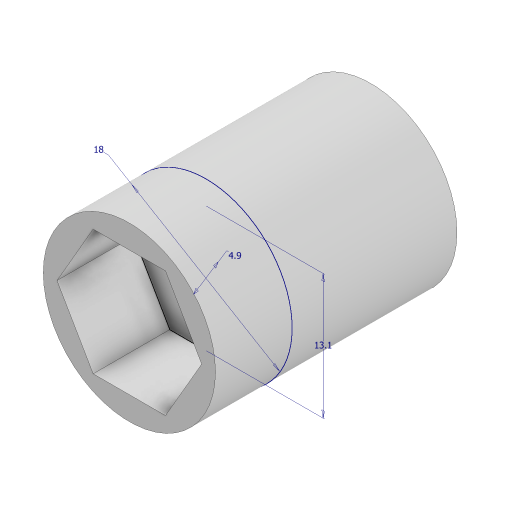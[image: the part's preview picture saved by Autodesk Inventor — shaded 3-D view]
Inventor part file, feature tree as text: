
AUTODESK INVENTOR PART (.ipt)
format: ipt  version: 2023 (Build 270158000, 158)  size: 139,264 bytes
history: native  units: mm
features: extrude x3, sketch x2
ambient origin geometry x8: Origin, YZ Plane, XZ Plane, XY Plane, X Axis, Y Axis, Z Axis, Center Point
bodies: Solid1 (feature_tree)
feature tree (5):
  sketch  "Sketch1"  dims[d0=13.1mm d1=18.0mm]
  extrude  "Extrusion1"  Depth=13.1mm
  extrude  "Extrusion2"  Depth=8.0mm TaperAngle=0.0deg
  extrude  "Extrusion3"  Depth=17.25mm TaperAngle=0.0deg
  sketch  "Sketch2"  dims[d2=4.9mm d3=8.0mm d4=0.0mm d5=17.25mm d6=0.0mm d7=10.0mm d8=12.75mm d9=0.0mm]
